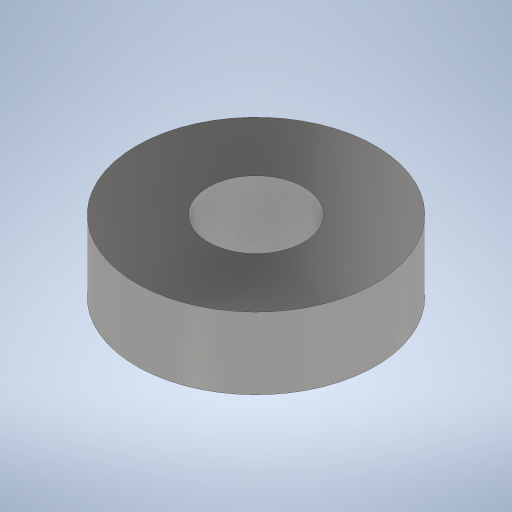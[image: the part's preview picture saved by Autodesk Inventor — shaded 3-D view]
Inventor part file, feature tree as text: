
AUTODESK INVENTOR PART (.ipt)
format: ipt  version: 2023.1 (Build 271208000, 208)  size: 225,280 bytes
history: native  units: mm
features: extrude x1, sketch x1
ambient origin geometry x8: Origin, YZ Plane, XZ Plane, XY Plane, X Axis, Y Axis, Z Axis, Center Point
bodies: Solid1 (feature_tree)
feature tree (2):
  extrude  "Extrusion1"  Depth=10.0mm
  sketch  "Sketch1"  dims[d0=4.0mm d1=10.0mm d2=3.0mm d3=0.0mm]
